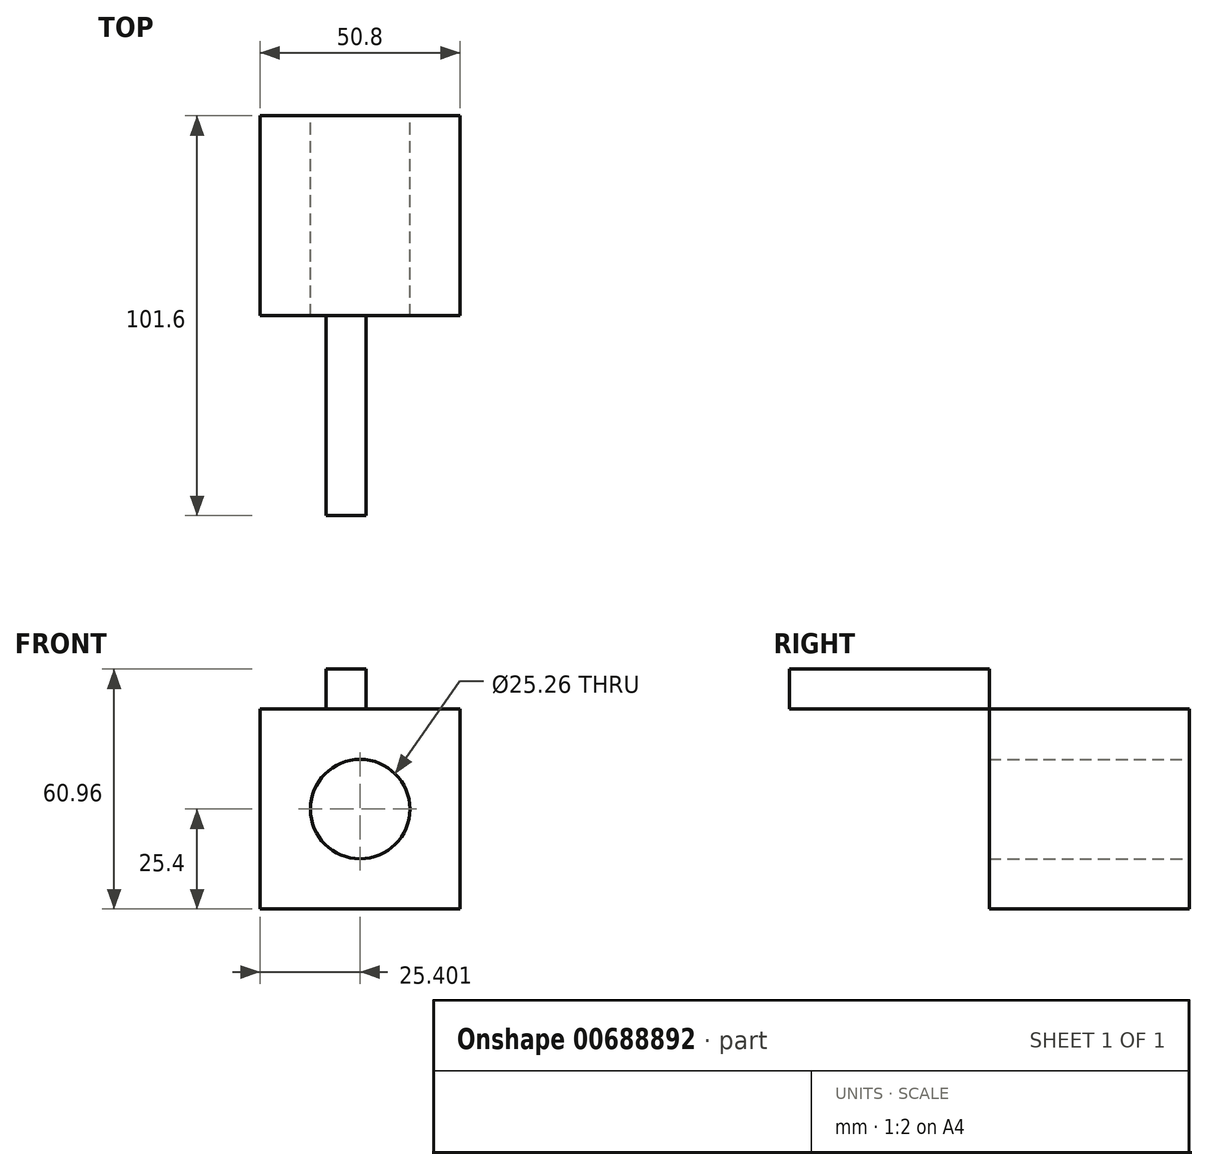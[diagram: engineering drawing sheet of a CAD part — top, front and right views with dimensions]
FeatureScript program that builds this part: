
annotation { "Feature Type Name" : "Feature", "Feature Type Description" : "" }
export const myFeature = defineFeature(function(context is Context, id is Id, definition is map)
    precondition{}
    {
        {
            var Q0;
            Q0=qCreatedBy(makeId("Front.planeOp"),FACE);
            var sketch = newSketch(context, id + "F0", { "sketchPlane" : qUnion([Q0])});
            skLineSegment(sketch, "E0", {"start": v(-66.89, 50.8) * mm, "end": v(-66.89, 0) * mm});
            skLineSegment(sketch, "E1", {"start": v(-66.89, 0) * mm, "end": v(-16.09, 0) * mm});
            skLineSegment(sketch, "E2", {"start": v(-16.09, 0) * mm, "end": v(-16.09, 50.8) * mm});
            skLineSegment(sketch, "E3", {"start": v(-16.09, 50.8) * mm, "end": v(-66.89, 50.8) * mm});
            skCircle(sketch, "E4", {"center": v(-41.49, 25.4) * mm, "radius": 12.63 * mm});
            skLineSegment(sketch, "E5", {"start": v(-41.49, 25.4) * mm, "end": v(-41.49, 50.8) * mm});
            skLineSegment(sketch, "E6", {"start": v(-41.49, 25.4) * mm, "end": v(-16.09, 25.4) * mm});
            skLineSegment(sketch, "E7", {"start": v(-41.49, 25.4) * mm, "end": v(-41.49, 0) * mm});
            skLineSegment(sketch, "E8", {"start": v(-41.49, 25.4) * mm, "end": v(-66.89, 25.4) * mm});
            skSolve(sketch);
        }
        {
            var Q0;
            Q0 = qSketchRegion(id + "Frudbd8jIKmbs4j_0", true);
            var Q1;
            Q1 = qSketchRegion(id + "F0", true);
            extrude(context, id + "F1", {"entities" : qUnion([Q0, Q1]), "depth" : 50.8 * mm, "offsetDistance" : 25.4 * mm});
        }
        {
            var Q0;
            Q0=makeQuery(id+"F1.opExtrude","CAP_FACE",FACE,{"disambiguationData":[OSD([sQuery(id+"F0.wireOp",EDGE,"E0"),sQuery(id+"F0.wireOp",EDGE,"E1"),sQuery(id+"F0.wireOp",EDGE,"E2"),sQuery(id+"F0.wireOp",EDGE,"E3"),sQuery(id+"F0.wireOp",EDGE,"E4")])],"isStart":false});
            var sketch = newSketch(context, id + "F2", { "sketchPlane" : qUnion([Q0])});
            skLineSegment(sketch, "E9", {"start": v(-50.12, 50.8) * mm, "end": v(-50.12, 60.96) * mm});
            skLineSegment(sketch, "E10", {"start": v(-50.12, 60.96) * mm, "end": v(-39.96, 60.96) * mm});
            skLineSegment(sketch, "E11", {"start": v(-39.96, 60.96) * mm, "end": v(-39.96, 50.8) * mm});
            skSolve(sketch);
        }
        {
            var Q0;
            {var subQ0=sQuery(id+"F2.wireOp",EDGE,"E9");Q0=makeQuery(id+"F2.imprint","IMPRINT",FACE,{"disambiguationData":[TD([[makeQuery(id+"F2.imprint","IMPRINT",EDGE,{"derivedFrom":subQ0}),-1.0]])]});}
            extrude(context, id + "F3", {"entities" : qUnion([Q0]), "depth" : 50.8 * mm, "offsetDistance" : 25.4 * mm});
        }
    });
